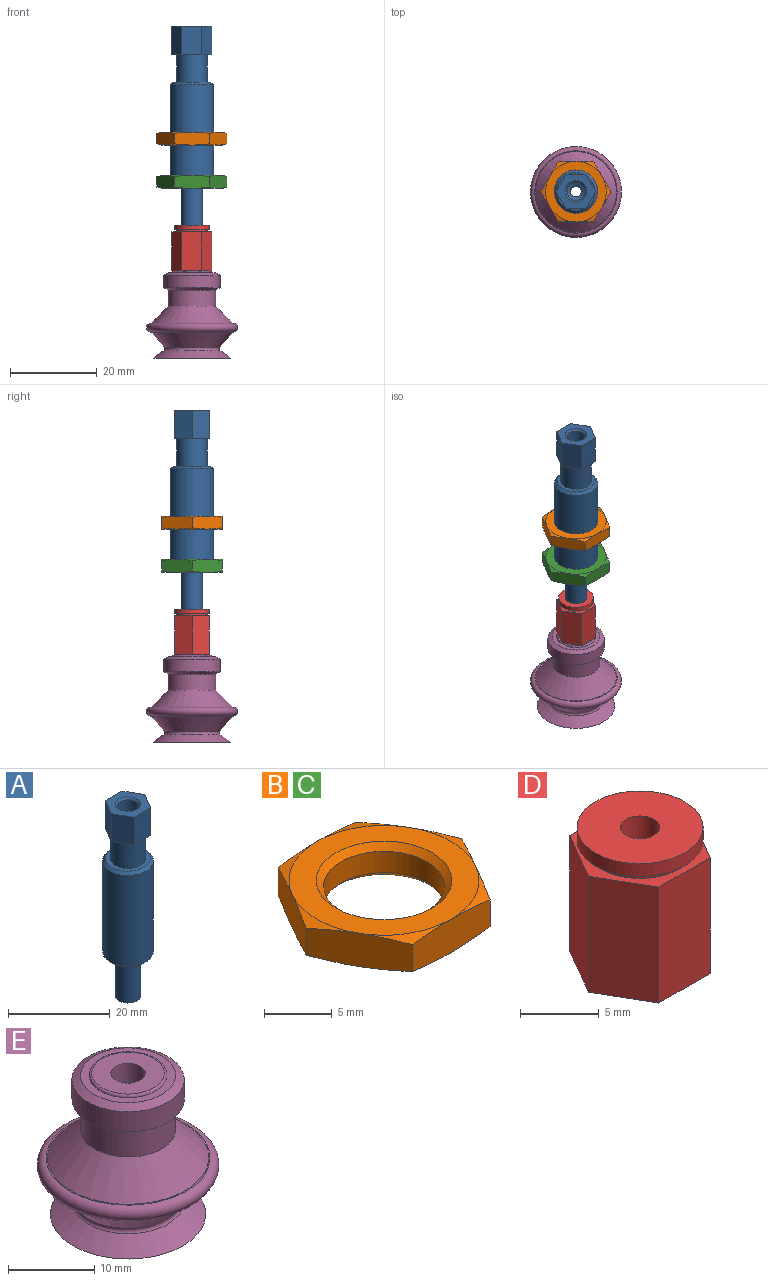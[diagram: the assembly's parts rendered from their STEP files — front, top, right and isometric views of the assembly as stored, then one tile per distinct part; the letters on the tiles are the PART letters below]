
ASSEMBLY  parts=5 mates=4
PART A: 20 faces, bbox 10x10x46 mm
  f0: plane 8.77x8.77mm, normal (0,0,1), area 22mm2, adj f1,f7
  f1: cone r=4.39mm half-angle=45deg, axis (0,0,-1), area 25.6mm2, adj f0,f2
  f2: cylinder r=5mm len=21.77mm, axis (0,0,-1), area 684mm2, adj f1,f3
  f3: cone r=5mm half-angle=45deg, axis (0,0,1), area 25.6mm2, adj f2,f4
  f4: plane 8.77x8.77mm, normal (0,0,-1), area 40.8mm2, adj f3,f5
  f5: cylinder r=2.5mm len=10mm, axis (0,0,-1), area 157.1mm2, adj f4,f6
  f6: plane 5x5mm, normal (0,0,-1), area 14.7mm2, adj f5,f19
  f7: cylinder r=3.5mm len=7mm, axis (0,0,-1), area 139.6mm2, adj f0,f15
  f8: plane 6.65x4mm, normal (-0.87,0.5,0), area 30.7mm2, adj f9,f13,f14,f15
  f9: plane 6.65x4mm, normal (-0.87,-0.5,0), area 30.7mm2, adj f8,f10,f14,f15
  f10: plane 6.65x4.62mm, normal (0,-1,0), area 30.7mm2, adj f9,f11,f14,f15
  f11: plane 6.65x4mm, normal (0.87,-0.5,0), area 30.7mm2, adj f10,f12,f14,f15
  f12: plane 6.65x4mm, normal (0.87,0.5,0), area 30.7mm2, adj f11,f13,f14,f15
  f13: plane 6.65x4.62mm, normal (0,1,0), area 30.7mm2, adj f8,f12,f14,f15
  f14: plane 9.24x8mm, normal (0,0,1), area 35.8mm2, adj f8,f9,f10,f11,f12,f13,f16
  f15: plane 9.24x8mm, normal (0,0,-1), area 16.9mm2, adj f7,f8,f9,f10,f11,f12,f13
  f16: cone r=2.5mm half-angle=45deg, axis (0,0,1), area 8.8mm2, adj f14,f17
  f17: cylinder r=2.07mm len=4.57mm, axis (0,0,-1), area 59.3mm2, adj f16,f18
  f18: cone r=2.07mm half-angle=60deg, axis (0,0,1), area 9.8mm2, adj f17,f19
  f19: cylinder r=1.25mm len=40.53mm, axis (0,0,-1), area 318.3mm2, adj f6,f18
PART B: 23 faces, bbox 16.8x16.8x3.6 mm
  f0: cone r=7mm half-angle=75deg, axis (0,0,1), area 4.3mm2, adj f13,f18,f19
  f1: cone r=7mm half-angle=75deg, axis (0,0,1), area 4.3mm2, adj f13,f19,f20
  f2: cone r=7mm half-angle=75deg, axis (0,0,1), area 4.3mm2, adj f13,f17,f18
  f3: cone r=7mm half-angle=75deg, axis (0,0,1), area 4.3mm2, adj f13,f20,f21
  f4: cone r=7mm half-angle=75deg, axis (0,0,1), area 4.3mm2, adj f13,f17,f22
  f5: cone r=9.6mm half-angle=75deg, axis (0,0,-1), area 4.3mm2, adj f16,f17,f22
  f6: cone r=9.6mm half-angle=75deg, axis (0,0,-1), area 4.3mm2, adj f16,f17,f18
  f7: cone r=9.6mm half-angle=75deg, axis (0,0,-1), area 4.3mm2, adj f16,f18,f19
  f8: cone r=9.6mm half-angle=75deg, axis (0,0,-1), area 4.3mm2, adj f16,f19,f20
  f9: cone r=9.6mm half-angle=75deg, axis (0,0,-1), area 4.3mm2, adj f16,f20,f21
  f10: cone r=5mm half-angle=45deg, axis (0,0,1), area 22.8mm2, adj f11,f16
  f11: cylinder r=4.46mm len=8.92mm, axis (0,0,-1), area 53.7mm2, adj f10,f12
  f12: cone r=4.46mm half-angle=45deg, axis (0,0,-1), area 22.8mm2, adj f11,f13
  f13: plane 14x14mm, normal (0,0,-1), area 75.4mm2, adj f0,f1,f2,f3,f4,f12,f14
  f14: cone r=7mm half-angle=75deg, axis (0,0,1), area 4.3mm2, adj f13,f21,f22
  f15: cone r=9.6mm half-angle=75deg, axis (0,0,-1), area 4.3mm2, adj f16,f21,f22
  f16: plane 14x14mm, normal (0,0,1), area 75.4mm2, adj f5,f6,f7,f8,f9,f10,f15
  f17: plane 7.6x4.64mm, normal (-0.87,0.5,0), area 22.6mm2, adj f2,f4,f5,f6,f18,f22
  f18: plane 8.69x3.6mm, normal (0,1,0), area 22.6mm2, adj f0,f2,f6,f7,f17,f19
  f19: plane 7.6x4.64mm, normal (0.87,0.5,0), area 22.6mm2, adj f0,f1,f7,f8,f18,f20
  f20: plane 7.6x4.64mm, normal (0.87,-0.5,0), area 22.6mm2, adj f1,f3,f8,f9,f19,f21
  f21: plane 8.69x3.6mm, normal (0,-1,0), area 22.6mm2, adj f3,f9,f14,f15,f20,f22
  f22: plane 7.6x4.64mm, normal (-0.87,-0.5,0), area 22.6mm2, adj f4,f5,f14,f15,f17,f21
PART C: same geometry as B
PART D: 13 faces, bbox 9.2x8x10.5 mm
  f0: plane 9x4mm, normal (-0.87,0.5,0), area 41.6mm2, adj f1,f5,f6,f7
  f1: plane 9x4mm, normal (-0.87,-0.5,0), area 41.6mm2, adj f0,f2,f6,f7
  f2: plane 9x4.62mm, normal (0,-1,0), area 41.6mm2, adj f1,f3,f6,f7
  f3: plane 9x4mm, normal (0.87,-0.5,0), area 41.6mm2, adj f2,f4,f6,f7
  f4: plane 9x4mm, normal (0.87,0.5,0), area 41.6mm2, adj f3,f5,f6,f7
  f5: plane 9x4.62mm, normal (0,1,0), area 41.6mm2, adj f0,f4,f6,f7
  f6: plane 9.24x8mm, normal (0,0,1), area 16.9mm2, adj f0,f1,f2,f3,f4,f5,f11
  f7: plane 9.24x8mm, normal (0,0,-1), area 50.5mm2, adj f0,f1,f2,f3,f4,f5,f12
  f8: plane 8x8mm, normal (0,0,1), area 45.4mm2, adj f9,f12
  f9: cylinder r=4mm len=8mm, axis (0,0,-1), area 25.1mm2, adj f8,f10
  f10: plane 8x8mm, normal (0,0,-1), area 11.8mm2, adj f9,f11
  f11: cylinder r=3.5mm len=7mm, axis (0,0,-1), area 11mm2, adj f6,f10
  f12: cylinder r=1.25mm len=10.5mm, axis (0,0,-1), area 82.5mm2, adj f7,f8
PART E: 22 faces, bbox 22.8x22.8x20 mm
  f0: plane 8.4x8.4mm, normal (0,0,1), area 42.9mm2, adj f1,f15
  f1: torus R=4.2mm, axis (0,0,-1), area 13.2mm2, adj f0,f2
  f2: plane 11x11mm, normal (0,0,1), area 31.4mm2, adj f1,f3
  f3: cone r=5.5mm half-angle=60deg, axis (0,0,-1), area 43.5mm2, adj f2,f4
  f4: cylinder r=6.5mm len=13mm, axis (0,0,-1), area 116.2mm2, adj f3,f5
  f5: cone r=6.5mm half-angle=60deg, axis (0,0,1), area 43.5mm2, adj f4,f6
  f6: cylinder r=5.5mm len=11mm, axis (0,0,-1), area 127.6mm2, adj f5,f7
  f7: cone r=5.5mm half-angle=43.8deg, axis (0,0,-1), area 258.5mm2, adj f6,f8
  f8: cone r=9.34mm half-angle=90deg, axis (0,0,-1), area 9.5mm2, adj f7,f9
  f9: torus R=9.51mm, axis (0,0,-1), area 200.3mm2, adj f8,f10
  f10: plane 19.04x19.04mm, normal (0,0,-1), area 5.8mm2, adj f9,f11
  f11: cone r=9.42mm half-angle=41.3deg, axis (0,0,1), area 229.8mm2, adj f10,f12
  f12: torus R=6.74mm, axis (0,0,-1), area 33.3mm2, adj f11,f13
  f13: cone r=6.45mm half-angle=55deg, axis (0,0,-1), area 150.8mm2, adj f12,f14
  f14: plane 18x18mm, normal (0,0,-1), area 53.4mm2, adj f13,f21
  f15: cylinder r=2mm len=11.5mm, axis (0,0,-1), area 144.5mm2, adj f0,f16
  f16: plane 13.88x13.88mm, normal (0,0,-1), area 138.7mm2, adj f15,f17
  f17: cone r=6.94mm half-angle=50deg, axis (0,0,-1), area 52.7mm2, adj f16,f18
  f18: torus R=7.04mm, axis (0,0,-1), area 95.8mm2, adj f17,f19
  f19: cone r=7.96mm half-angle=39.7deg, axis (0,0,1), area 179.9mm2, adj f18,f20
  f20: torus R=5.8mm, axis (0,0,-1), area 44.5mm2, adj f19,f21
  f21: cone r=5.39mm half-angle=59.6deg, axis (0,0,-1), area 127.1mm2, adj f14,f20
PLACE A at identity
PLACE B t=(0,0,50.5)mm
PLACE C rot(axis=(1,0,0),180deg) t=(0,0,40.5)mm
PLACE D t=(0,0,20)mm
PLACE E t=(0,0,-0.19)mm
MATE fastened C.f0 <-> A.f1  axis (0,0,1) through (0,0,42)mm
MATE fastened E.f3 <-> D.f9  axis (0,0,1) through (0,0,19.5)mm
MATE fastened B.f0 <-> A.f1  axis (0,0,1) through (0,0,52)mm
MATE fastened A.f1 <-> D.f9  axis (0,0,-1) through (0,0,30.5)mm
